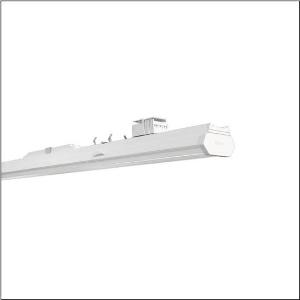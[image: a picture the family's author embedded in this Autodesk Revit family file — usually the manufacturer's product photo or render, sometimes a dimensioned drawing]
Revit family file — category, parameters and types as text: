
# Revit family: licross_r__21_protected_mo_52tp12dn4a5g3s4_4701
name_source: partatom
category: Lighting Fixtures
units: mm (PartAtom-declared; Revit-internal decimal feet)

## family parameters
Cut with Voids When Loaded = No
Host = Face
Light Source = No
Part Type = Normal
Room Calculation Point = No
Round Connector Dimension = Use Diameter
Shared = No

## types (1)
- --- (1 x LED, 940 lm, 6.8 W, 4000K)
    Apparent Load = 7 VA
    CIE Flux Codes = 73 92 98 99 100
    Color Rendering = 80
    Color Temperature = 4000K
    Default Elevation = 1800 mm
    Description = Licross® 21 Protected MO, luminaire insert, of sheet steel, galvanised, coil coated, white, length: 1.500mm, width: 90mm, height: 103mm, LED rated luminous flux: 10.700lm, light colour: 840, SDCM (Standard Deviation of Colour Matching)MacAdam ≤ 3 SDCM (initial), control gear: DALI 2, with plug, 6-pole, with phase selection, for trunking rail, 9 or 11-core, mains connection: 220..240V, AC, 50/60Hz, rated input power: 66W, for trunking rail, 9-/11-core, internal wiring halogen-free, for emergency light function, converter,control gear: single battery element, battery: LiFePO4, 9Ah, primary light control with lens, of plastic, primary optical cover: cover, of PMMA, light emission: direct distribution, primary light characteristic: symmetric, protection rating (complete): IP64, insulation class (complete): insulation class I (protective earthing), certification: CE, UKCA, protection symbol: D if used in an environment with conductive dust loads with corresponding accessories, impact resistance: IK06, permissible ambient temperature for indoor applications: +5..+35°C, standard: EN 60598-2-22, LABS conformity tested according to VDMA 24364:2018-05, reducing of maximum allowable ambient temperature of 5°C with ceiling mounting, corresponds to IFS (International Featured Standards) requirements for safety and quality in the food industry, packaging unit: 1 piece
    Height = 92 mm
    Lamp = 1 x LED
    Lamp Light Flux = 940 lm
    Lamp Power = 6.8 W
    Lamp count = 1
    Length = 1500 mm
    Luminous efficacy = 138 lm/W
    Manufacturer = Siteco
    ModVariant = No
    Model = 52TP12DN4A5G3S4
    Mounting Place = Ceiling
    Mounting Type = Pendant
    Number of Poles = 1
    OnlyDefault = Yes
    Power Factor = 1
    Product Name = Licross® 21 Protected MO
    Product group = luminaire insert | ceiling pendant
    ProductGroupID = 901
    Protection Class = Protection class I
    Protection Degree = IP 64
    RLX_Detail_Level = 1
    RLX_Emergency_Light_Flux = 0 lm
    RLX_Emergency_Type = 0
    RLX_Emergency_Type_DB = No
    RlxData = <blob elided: 24941 chars, md5=923ab2ed>
    Socket = socket
    Standby Power = 0 W
    System Light Flux = 940 lm
    System Power = 7 W
    Type Comments = : emergency light operation: 3 h
    Type Image = l_1256148.jpg
    URL = http://relux.com
    VarID = @adj_114831
    Voltage = 0 V
    Weight = 0.00 kg
    Width = 88 mm

## geometry (parser evidence)
native form markers: Blend x4, Sweep x9
no freeform markers — native parametric forms only
